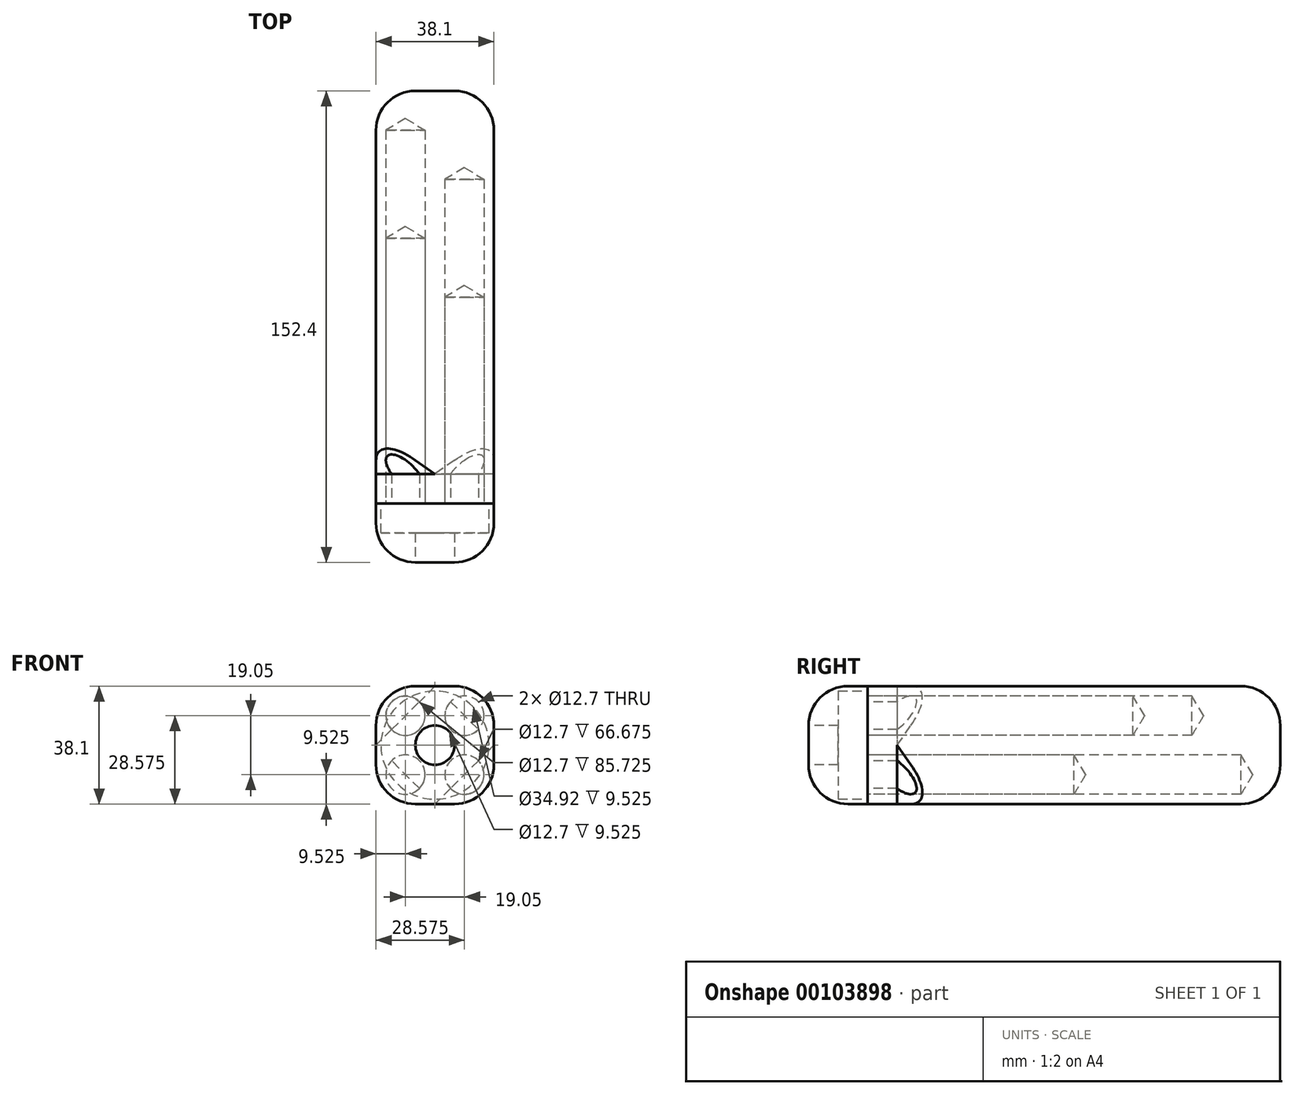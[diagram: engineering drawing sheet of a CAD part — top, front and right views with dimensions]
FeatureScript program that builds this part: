
annotation { "Feature Type Name" : "Feature", "Feature Type Description" : "" }
export const myFeature = defineFeature(function(context is Context, id is Id, definition is map)
    precondition{}
    {
        {
            var Q0;
            Q0=qCreatedBy(makeId("Front.planeOp"),FACE);
            var sketch = newSketch(context, id + "F0", { "sketchPlane" : qUnion([Q0])});
            skLineSegment(sketch, "E0.bottom", {"start": v(6.35, 19.05) * mm, "end": v(-6.35, 19.05) * mm});
            skLineSegment(sketch, "E0.top", {"start": v(6.35, -19.05) * mm, "end": v(-6.35, -19.05) * mm});
            skLineSegment(sketch, "E0.left", {"start": v(19.05, 6.35) * mm, "end": v(19.05, -6.35) * mm});
            skLineSegment(sketch, "E0.right", {"start": v(-19.05, 6.35) * mm, "end": v(-19.05, -6.35) * mm});
            skPoint(sketch, "E0.middle", {"position": v(0, 0) * mm});
            skPoint(sketch, "E1.visualSharp", {"position": v(-19.05, 19.05) * mm});
            skArc(sketch, "E1.filletArc", {"start": v(-6.35, 19.05) * mm, "mid": v(-15.33, 15.33) * mm, "end": v(-19.05, 6.35) * mm});
            skPoint(sketch, "E2.visualSharp", {"position": v(19.05, 19.05) * mm});
            skArc(sketch, "E2.filletArc", {"start": v(19.05, 6.35) * mm, "mid": v(15.33, 15.33) * mm, "end": v(6.35, 19.05) * mm});
            skPoint(sketch, "E3.visualSharp", {"position": v(19.05, -19.05) * mm});
            skArc(sketch, "E3.filletArc", {"start": v(6.35, -19.05) * mm, "mid": v(15.33, -15.33) * mm, "end": v(19.05, -6.35) * mm});
            skPoint(sketch, "E4.visualSharp", {"position": v(-19.05, -19.05) * mm});
            skArc(sketch, "E4.filletArc", {"start": v(-19.05, -6.35) * mm, "mid": v(-15.33, -15.33) * mm, "end": v(-6.35, -19.05) * mm});
            skSolve(sketch);
        }
        {
            var Q0;
            Q0=makeQuery(id+"F0.imprint","IMPRINT",FACE,{"disambiguationData":[TD([[makeQuery(id+"F0.imprint","IMPRINT",EDGE,{"derivedFrom":sQuery(id+"F0.wireOp",EDGE,"E0.bottom")}),1.0]])]});
            extrude(context, id + "F1", {"entities" : qUnion([Q0]), "depth" : 133.35 * mm});
        }
        {
            var Q0;
            Q0=makeQuery(id+"F1.opExtrude","CAP_FACE",FACE,{"disambiguationData":[OSD([sQuery(id+"F0.wireOp",EDGE,"E0.bottom"),sQuery(id+"F0.wireOp",EDGE,"E0.top"),sQuery(id+"F0.wireOp",EDGE,"E0.left"),sQuery(id+"F0.wireOp",EDGE,"E0.right"),sQuery(id+"F0.wireOp",EDGE,"E1.filletArc"),sQuery(id+"F0.wireOp",EDGE,"E2.filletArc"),sQuery(id+"F0.wireOp",EDGE,"E3.filletArc"),sQuery(id+"F0.wireOp",EDGE,"E4.filletArc")])],"isStart":false});
            var sketch = newSketch(context, id + "F2", { "sketchPlane" : qUnion([Q0])});
            skCircle(sketch, "E5", {"center": v(-9.53, -9.52) * mm, "radius": 6.35 * mm});
            skCircle(sketch, "E6.1.0.0", {"center": v(9.53, -9.52) * mm, "radius": 6.35 * mm});
            skLineSegment(sketch, "E6.direction1", {"start": v(-9.53, -9.52) * mm, "end": v(9.53, -9.52) * mm, "construction": true});
            skCircle(sketch, "E7.MirrorC", {"center": v(-9.53, 9.52) * mm, "radius": 6.35 * mm});
            skCircle(sketch, "E8.MirrorC", {"center": v(9.53, 9.52) * mm, "radius": 6.35 * mm});
            skSolve(sketch);
        }
        {
            var Q0;
            Q0=sQuery(id+"F2.wireOp",VERTEX,"E6.direction1.start");
            var Q1;
            Q1=makeQuery(id+"F1.opExtrude","SWEPT_BODY",BODY,{"disambiguationData":[OSD([sQuery(id+"F0.wireOp",EDGE,"E0.bottom"),sQuery(id+"F0.wireOp",EDGE,"E0.top"),sQuery(id+"F0.wireOp",EDGE,"E0.left"),sQuery(id+"F0.wireOp",EDGE,"E0.right"),sQuery(id+"F0.wireOp",EDGE,"E1.filletArc"),sQuery(id+"F0.wireOp",EDGE,"E2.filletArc"),sQuery(id+"F0.wireOp",EDGE,"E3.filletArc"),sQuery(id+"F0.wireOp",EDGE,"E4.filletArc")])]});
            hole(context, id + "F3", {"style" : HoleStyle.SIMPLE, "endStyle" : HoleEndStyle.BLIND, "holeDiameter" : 12.7 * mm, "majorDiameter" : 6.35 * mm, "holeDepth" : 120.65 * mm, "locations" : qUnion([Q0]), "scope" : qUnion([Q1]), "tappedDepth" : 12.7 * mm, "tapClearance" : 3});
        }
        {
            var Q0;
            Q0=sQuery(id+"F2.wireOp",VERTEX,"E8.MirrorC.center");
            var Q1;
            Q1=makeQuery(id+"F1.opExtrude","SWEPT_BODY",BODY,{"disambiguationData":[OSD([sQuery(id+"F0.wireOp",EDGE,"E0.bottom"),sQuery(id+"F0.wireOp",EDGE,"E0.top"),sQuery(id+"F0.wireOp",EDGE,"E0.left"),sQuery(id+"F0.wireOp",EDGE,"E0.right"),sQuery(id+"F0.wireOp",EDGE,"E1.filletArc"),sQuery(id+"F0.wireOp",EDGE,"E2.filletArc"),sQuery(id+"F0.wireOp",EDGE,"E3.filletArc"),sQuery(id+"F0.wireOp",EDGE,"E4.filletArc")])]});
            hole(context, id + "F4", {"style" : HoleStyle.SIMPLE, "endStyle" : HoleEndStyle.BLIND, "holeDiameter" : 12.7 * mm, "holeDepth" : 104.77 * mm, "locations" : qUnion([Q0]), "scope" : qUnion([Q1])});
        }
        {
            var Q0;
            Q0=sQuery(id+"F2.wireOp",VERTEX,"E7.MirrorC.center");
            var Q1;
            Q1=makeQuery(id+"F1.opExtrude","SWEPT_BODY",BODY,{"disambiguationData":[OSD([sQuery(id+"F0.wireOp",EDGE,"E0.bottom"),sQuery(id+"F0.wireOp",EDGE,"E0.top"),sQuery(id+"F0.wireOp",EDGE,"E0.left"),sQuery(id+"F0.wireOp",EDGE,"E0.right"),sQuery(id+"F0.wireOp",EDGE,"E1.filletArc"),sQuery(id+"F0.wireOp",EDGE,"E2.filletArc"),sQuery(id+"F0.wireOp",EDGE,"E3.filletArc"),sQuery(id+"F0.wireOp",EDGE,"E4.filletArc")])]});
            hole(context, id + "F5", {"style" : HoleStyle.SIMPLE, "endStyle" : HoleEndStyle.BLIND, "holeDiameter" : 12.7 * mm, "holeDepth" : 85.72 * mm, "locations" : qUnion([Q0]), "scope" : qUnion([Q1])});
        }
        {
            var Q0;
            Q0=sQuery(id+"F2.wireOp",VERTEX,"E6.1.0.0.center");
            var Q1;
            Q1=makeQuery(id+"F1.opExtrude","SWEPT_BODY",BODY,{"disambiguationData":[OSD([sQuery(id+"F0.wireOp",EDGE,"E0.bottom"),sQuery(id+"F0.wireOp",EDGE,"E0.top"),sQuery(id+"F0.wireOp",EDGE,"E0.left"),sQuery(id+"F0.wireOp",EDGE,"E0.right"),sQuery(id+"F0.wireOp",EDGE,"E1.filletArc"),sQuery(id+"F0.wireOp",EDGE,"E2.filletArc"),sQuery(id+"F0.wireOp",EDGE,"E3.filletArc"),sQuery(id+"F0.wireOp",EDGE,"E4.filletArc")])]});
            hole(context, id + "F6", {"style" : HoleStyle.SIMPLE, "endStyle" : HoleEndStyle.BLIND, "holeDiameter" : 12.7 * mm, "holeDepth" : 66.67 * mm, "locations" : qUnion([Q0]), "scope" : qUnion([Q1])});
        }
        {
            var Q0;
            Q0=makeQuery(id+"F2.imprint","IMPRINT",FACE,{"disambiguationData":[TD([[makeQuery(id+"F2.imprint","IMPRINT",EDGE,{"derivedFrom":sQuery(id+"F2.wireOp",EDGE,"E5")}),-1.0]])]});
            cPlane(context, id + "F7", {"entities" : qUnion([Q0]), "cplaneType" : CPlaneType.OFFSET, "offset" : 9.52 * mm, "oppositeDirection" : true, "width" : 152.4 * mm, "height" : 152.4 * mm});
        }
        {
            var Q0;
            Q0=qCreatedBy(id+"F7.planeOp",FACE);
            var sketch = newSketch(context, id + "F8", { "sketchPlane" : qUnion([Q0])});
            skLineSegment(sketch, "E9", {"start": v(0, 19.05) * mm, "end": v(19.05, 0) * mm});
            skLineSegment(sketch, "E10", {"start": v(19.05, 0) * mm, "end": v(0, -19.05) * mm});
            skLineSegment(sketch, "E11", {"start": v(0, -19.05) * mm, "end": v(-19.05, 0) * mm});
            skLineSegment(sketch, "E12", {"start": v(-19.05, 0) * mm, "end": v(0, 19.05) * mm});
            skSolve(sketch);
        }
        {
            var Q0;
            Q0=sQuery(id+"F8.wireOp",EDGE,"E12");
            cPlane(context, id + "F9", {"entities" : qUnion([Q0]), "cplaneType" : CPlaneType.MID_PLANE, "offset" : 152.4 * mm, "width" : 152.4 * mm, "height" : 152.4 * mm});
        }
        {
            var Q0;
            Q0=qCreatedBy(id+"F9.planeOp",FACE);
            var sketch = newSketch(context, id + "F10", { "sketchPlane" : qUnion([Q0])});
            skLineSegment(sketch, "E13", {"start": v(-123.83, 13.47) * mm, "end": v(-123.83, 64.27) * mm});
            skLineSegment(sketch, "E14", {"start": v(-123.83, 64.27) * mm, "end": v(-73.03, 64.27) * mm});
            skLineSegment(sketch, "E15", {"start": v(-73.03, 64.27) * mm, "end": v(-123.83, 13.47) * mm});
            skLineSegment(sketch, "E16.MirrorCS", {"start": v(-73.03, -64.27) * mm, "end": v(-123.83, -13.47) * mm});
            skLineSegment(sketch, "E17.MirrorCS", {"start": v(-123.83, -13.47) * mm, "end": v(-123.83, -64.27) * mm});
            skLineSegment(sketch, "E18.MirrorCS", {"start": v(-123.83, -64.27) * mm, "end": v(-73.03, -64.27) * mm});
            skSolve(sketch);
        }
        {
            var Q0;
            Q0=makeQuery(id+"F10.imprint","IMPRINT",FACE,{"disambiguationData":[TD([[makeQuery(id+"F10.imprint","IMPRINT",EDGE,{"derivedFrom":sQuery(id+"F10.wireOp",EDGE,"E13")}),-1.0]])]});
            var Q1;
            Q1=makeQuery(id+"F10.imprint","IMPRINT",FACE,{"disambiguationData":[TD([[makeQuery(id+"F10.imprint","IMPRINT",EDGE,{"derivedFrom":sQuery(id+"F10.wireOp",EDGE,"E16.MirrorCS")}),1.0]])]});
            extrude(context, id + "F11", {"entities" : qUnion([Q0, Q1]), "operationType" : NewBodyOperationType.REMOVE, "depth" : 31.24 * mm, "symmetric" : true});
        }
        {
            var Q0;
            Q0=sQuery(id+"F8.wireOp",EDGE,"E9");
            cPlane(context, id + "F12", {"entities" : qUnion([Q0]), "cplaneType" : CPlaneType.MID_PLANE, "offset" : 152.4 * mm, "width" : 152.4 * mm, "height" : 152.4 * mm});
        }
        {
            var Q0;
            Q0=qCreatedBy(id+"F12.planeOp",FACE);
            var sketch = newSketch(context, id + "F13", { "sketchPlane" : qUnion([Q0])});
            skLineSegment(sketch, "E19", {"start": v(13.47, 123.83) * mm, "end": v(38.87, 123.83) * mm});
            skLineSegment(sketch, "E20", {"start": v(38.87, 123.83) * mm, "end": v(38.87, 98.43) * mm});
            skLineSegment(sketch, "E21", {"start": v(38.87, 98.42) * mm, "end": v(13.47, 123.83) * mm});
            skLineSegment(sketch, "E22.MirrorCS", {"start": v(-38.87, 98.42) * mm, "end": v(-13.47, 123.83) * mm});
            skLineSegment(sketch, "E23.MirrorCS", {"start": v(-13.47, 123.83) * mm, "end": v(-38.87, 123.83) * mm});
            skLineSegment(sketch, "E24.MirrorCS", {"start": v(-38.87, 123.83) * mm, "end": v(-38.87, 98.43) * mm});
            skSolve(sketch);
        }
        {
            var Q0;
            Q0 = qSketchRegion(id + "F13", true);
            extrude(context, id + "F14", {"entities" : qUnion([Q0]), "operationType" : NewBodyOperationType.REMOVE, "depth" : 31.75 * mm, "symmetric" : true});
        }
        {
            var Q0;
            Q0=makeQuery(id+"F1.opExtrude","CAP_FACE",FACE,{"disambiguationData":[OSD([sQuery(id+"F0.wireOp",EDGE,"E0.bottom"),sQuery(id+"F0.wireOp",EDGE,"E0.top"),sQuery(id+"F0.wireOp",EDGE,"E0.left"),sQuery(id+"F0.wireOp",EDGE,"E0.right"),sQuery(id+"F0.wireOp",EDGE,"E1.filletArc"),sQuery(id+"F0.wireOp",EDGE,"E2.filletArc"),sQuery(id+"F0.wireOp",EDGE,"E3.filletArc"),sQuery(id+"F0.wireOp",EDGE,"E4.filletArc")])],"isStart":false});
            cPlane(context, id + "F15", {"entities" : qUnion([Q0]), "cplaneType" : CPlaneType.OFFSET, "offset" : 0 * mm, "width" : 152.4 * mm, "height" : 152.4 * mm});
        }
        {
            var Q0;
            Q0=qCreatedBy(id+"F15.planeOp",FACE);
            var sketch = newSketch(context, id + "F16", { "sketchPlane" : qUnion([Q0])});
            skLineSegment(sketch, "E25", {"start": v(-14.02, 5.03) * mm, "end": v(-5.03, 14.02) * mm});
            skLineSegment(sketch, "E26", {"start": v(5.03, 14.02) * mm, "end": v(14.02, 5.03) * mm});
            skLineSegment(sketch, "E27", {"start": v(14.02, -5.03) * mm, "end": v(5.03, -14.02) * mm});
            skLineSegment(sketch, "E28", {"start": v(-5.03, -14.02) * mm, "end": v(-14.02, -5.03) * mm});
            skArc(sketch, "E29", {"start": v(5.03, 14.02) * mm, "mid": v(5.03, 5.03) * mm, "end": v(14.02, 5.03) * mm});
            skArc(sketch, "E30", {"start": v(-5.03, -14.02) * mm, "mid": v(-5.03, -5.03) * mm, "end": v(-14.02, -5.03) * mm});
            skArc(sketch, "E31", {"start": v(14.02, -5.03) * mm, "mid": v(5.03, -5.03) * mm, "end": v(5.03, -14.02) * mm});
            skArc(sketch, "E32", {"start": v(-14.02, 5.03) * mm, "mid": v(-5.03, 5.03) * mm, "end": v(-5.03, 14.02) * mm});
            skPoint(sketch, "E33.orphan", {"position": v(-19.05, 0) * mm});
            skPoint(sketch, "E34.orphan", {"position": v(0, 19.05) * mm});
            skPoint(sketch, "E35.orphan", {"position": v(19.05, 0) * mm});
            skPoint(sketch, "E36.orphan", {"position": v(0, -19.05) * mm});
            skSolve(sketch);
        }
        {
            var Q0;
            Q0 = qSketchRegion(id + "F16", true);
            extrude(context, id + "F17", {"entities" : qUnion([Q0]), "oppositeDirection" : true, "depth" : 9.52 * mm});
        }
        {
            var Q0;
            Q0=makeQuery(id+"F1.opExtrude","CAP_FACE",FACE,{"disambiguationData":[OSD([sQuery(id+"F0.wireOp",EDGE,"E0.bottom"),sQuery(id+"F0.wireOp",EDGE,"E0.top"),sQuery(id+"F0.wireOp",EDGE,"E0.left"),sQuery(id+"F0.wireOp",EDGE,"E0.right"),sQuery(id+"F0.wireOp",EDGE,"E1.filletArc"),sQuery(id+"F0.wireOp",EDGE,"E2.filletArc"),sQuery(id+"F0.wireOp",EDGE,"E3.filletArc"),sQuery(id+"F0.wireOp",EDGE,"E4.filletArc")])],"isStart":false});
            cPlane(context, id + "F18", {"entities" : qUnion([Q0]), "cplaneType" : CPlaneType.OFFSET, "offset" : 19.05 * mm, "width" : 152.4 * mm, "height" : 152.4 * mm});
        }
        {
            var Q0;
            Q0=qCreatedBy(id+"F18.planeOp",FACE);
            var sketch = newSketch(context, id + "F19", { "sketchPlane" : qUnion([Q0])});
            skLineSegment(sketch, "E37.bottom", {"start": v(6.35, -19.05) * mm, "end": v(-6.35, -19.05) * mm});
            skLineSegment(sketch, "E37.top", {"start": v(6.35, 19.05) * mm, "end": v(-6.35, 19.05) * mm});
            skLineSegment(sketch, "E37.left", {"start": v(19.05, -6.35) * mm, "end": v(19.05, 6.35) * mm});
            skLineSegment(sketch, "E37.right", {"start": v(-19.05, -6.35) * mm, "end": v(-19.05, 6.35) * mm});
            skPoint(sketch, "E37.middle", {"position": v(0, 0) * mm});
            skPoint(sketch, "E38.visualSharp", {"position": v(-19.05, 19.05) * mm});
            skArc(sketch, "E38.filletArc", {"start": v(-6.35, 19.05) * mm, "mid": v(-15.33, 15.33) * mm, "end": v(-19.05, 6.35) * mm});
            skPoint(sketch, "E39.visualSharp", {"position": v(19.05, 19.05) * mm});
            skArc(sketch, "E39.filletArc", {"start": v(19.05, 6.35) * mm, "mid": v(15.33, 15.33) * mm, "end": v(6.35, 19.05) * mm});
            skPoint(sketch, "E40.visualSharp", {"position": v(19.05, -19.05) * mm});
            skArc(sketch, "E40.filletArc", {"start": v(6.35, -19.05) * mm, "mid": v(15.33, -15.33) * mm, "end": v(19.05, -6.35) * mm});
            skPoint(sketch, "E41.visualSharp", {"position": v(-19.05, -19.05) * mm});
            skArc(sketch, "E41.filletArc", {"start": v(-19.05, -6.35) * mm, "mid": v(-15.33, -15.33) * mm, "end": v(-6.35, -19.05) * mm});
            skSolve(sketch);
        }
        {
            var Q0;
            Q0=makeQuery(id+"F19.imprint","IMPRINT",FACE,{"disambiguationData":[TD([[makeQuery(id+"F19.imprint","IMPRINT",EDGE,{"derivedFrom":sQuery(id+"F19.wireOp",EDGE,"E37.bottom")}),-1.0]])]});
            extrude(context, id + "F20", {"entities" : qUnion([Q0]), "oppositeDirection" : true, "depth" : 19.05 * mm});
        }
        {
            var Q0;
            Q0=makeQuery(id+"F20.opExtrude","CAP_FACE",FACE,{"disambiguationData":[OSD([sQuery(id+"F19.wireOp",EDGE,"E37.bottom"),sQuery(id+"F19.wireOp",EDGE,"E37.top"),sQuery(id+"F19.wireOp",EDGE,"E37.left"),sQuery(id+"F19.wireOp",EDGE,"E37.right"),sQuery(id+"F19.wireOp",EDGE,"E38.filletArc"),sQuery(id+"F19.wireOp",EDGE,"E39.filletArc"),sQuery(id+"F19.wireOp",EDGE,"E40.filletArc"),sQuery(id+"F19.wireOp",EDGE,"E41.filletArc")])],"isStart":false});
            var sketch = newSketch(context, id + "F21", { "sketchPlane" : qUnion([Q0])});
            skCircle(sketch, "E42", {"center": v(0, 0) * mm, "radius": 17.46 * mm});
            skSolve(sketch);
        }
        {
            var Q0;
            Q0=makeQuery(id+"F21.imprint","IMPRINT",FACE,{"disambiguationData":[TD([[makeQuery(id+"F21.imprint","IMPRINT",EDGE,{"derivedFrom":sQuery(id+"F21.wireOp",EDGE,"E42")}),1.0]])]});
            extrude(context, id + "F22", {"entities" : qUnion([Q0]), "operationType" : NewBodyOperationType.REMOVE, "oppositeDirection" : true, "depth" : 9.52 * mm});
        }
        {
            var Q0;
            Q0=makeQuery(id+"F20.opExtrude","CAP_FACE",FACE,{"disambiguationData":[OSD([sQuery(id+"F19.wireOp",EDGE,"E37.bottom"),sQuery(id+"F19.wireOp",EDGE,"E37.top"),sQuery(id+"F19.wireOp",EDGE,"E37.left"),sQuery(id+"F19.wireOp",EDGE,"E37.right"),sQuery(id+"F19.wireOp",EDGE,"E38.filletArc"),sQuery(id+"F19.wireOp",EDGE,"E39.filletArc"),sQuery(id+"F19.wireOp",EDGE,"E40.filletArc"),sQuery(id+"F19.wireOp",EDGE,"E41.filletArc")])],"isStart":true});
            var sketch = newSketch(context, id + "F23", { "sketchPlane" : qUnion([Q0])});
            skPoint(sketch, "E43", {"position": v(0, 0) * mm});
            skSolve(sketch);
        }
        {
            var Q0;
            Q0=sQuery(id+"F23.wireOp",VERTEX,"E43");
            var Q1;
            Q1=makeQuery(id+"F20.opExtrude","SWEPT_BODY",BODY,{"disambiguationData":[OSD([sQuery(id+"F19.wireOp",EDGE,"E37.bottom"),sQuery(id+"F19.wireOp",EDGE,"E37.top"),sQuery(id+"F19.wireOp",EDGE,"E37.left"),sQuery(id+"F19.wireOp",EDGE,"E37.right"),sQuery(id+"F19.wireOp",EDGE,"E38.filletArc"),sQuery(id+"F19.wireOp",EDGE,"E39.filletArc"),sQuery(id+"F19.wireOp",EDGE,"E40.filletArc"),sQuery(id+"F19.wireOp",EDGE,"E41.filletArc")])]});
            hole(context, id + "F24", {"style" : HoleStyle.SIMPLE, "endStyle" : HoleEndStyle.BLIND, "holeDiameter" : 12.7 * mm, "holeDepth" : 9.52 * mm, "locations" : qUnion([Q0]), "scope" : qUnion([Q1])});
        }
        {
            var Q0;
            Q0=makeQuery(id+"F1.opExtrude","SWEPT_BODY",BODY,{"disambiguationData":[OSD([sQuery(id+"F0.wireOp",EDGE,"E0.bottom"),sQuery(id+"F0.wireOp",EDGE,"E0.top"),sQuery(id+"F0.wireOp",EDGE,"E0.left"),sQuery(id+"F0.wireOp",EDGE,"E0.right"),sQuery(id+"F0.wireOp",EDGE,"E1.filletArc"),sQuery(id+"F0.wireOp",EDGE,"E2.filletArc"),sQuery(id+"F0.wireOp",EDGE,"E3.filletArc"),sQuery(id+"F0.wireOp",EDGE,"E4.filletArc")])]});
            var Q1;
            Q1=makeQuery(id+"F17.opExtrude","SWEPT_BODY",BODY,{"disambiguationData":[OSD([sQuery(id+"F16.wireOp",EDGE,"E25"),sQuery(id+"F16.wireOp",EDGE,"E32")])]});
            var Q2;
            Q2=makeQuery(id+"F17.opExtrude","SWEPT_BODY",BODY,{"disambiguationData":[OSD([sQuery(id+"F16.wireOp",EDGE,"E26"),sQuery(id+"F16.wireOp",EDGE,"E29")])]});
            var Q3;
            Q3=makeQuery(id+"F17.opExtrude","SWEPT_BODY",BODY,{"disambiguationData":[OSD([sQuery(id+"F16.wireOp",EDGE,"E27"),sQuery(id+"F16.wireOp",EDGE,"E31")])]});
            var Q4;
            Q4=makeQuery(id+"F17.opExtrude","SWEPT_BODY",BODY,{"disambiguationData":[OSD([sQuery(id+"F16.wireOp",EDGE,"E28"),sQuery(id+"F16.wireOp",EDGE,"E30")])]});
            var Q5;
            Q5=makeQuery(id+"F20.opExtrude","SWEPT_BODY",BODY,{"disambiguationData":[OSD([sQuery(id+"F19.wireOp",EDGE,"E37.bottom"),sQuery(id+"F19.wireOp",EDGE,"E37.top"),sQuery(id+"F19.wireOp",EDGE,"E37.left"),sQuery(id+"F19.wireOp",EDGE,"E37.right"),sQuery(id+"F19.wireOp",EDGE,"E38.filletArc"),sQuery(id+"F19.wireOp",EDGE,"E39.filletArc"),sQuery(id+"F19.wireOp",EDGE,"E40.filletArc"),sQuery(id+"F19.wireOp",EDGE,"E41.filletArc")])]});
            booleanBodies(context, id + "F25", {"operationType" : BooleanOperationType.INTERSECTION, "tools" : qUnion([Q0, Q1, Q2, Q3, Q4, Q5]), "keepTools" : true});
        }
        {
            var Q0;
            Q0=makeQuery(id+"F1.opExtrude","CAP_EDGE",EDGE,{"disambiguationData":[OSD([sQuery(id+"F0.wireOp",EDGE,"E0.bottom")])],"isStart":true});
            var Q1;
            Q1=makeQuery(id+"F20.opExtrude","CAP_EDGE",EDGE,{"disambiguationData":[OSD([sQuery(id+"F19.wireOp",EDGE,"E37.top")])],"isStart":true});
            fillet(context, id + "F26", {"entities" : qUnion([Q0, Q1]), "radius" : 12.7 * mm, "tangentPropagation" : true, "allowEdgeOverflow" : false});
        }
    });
